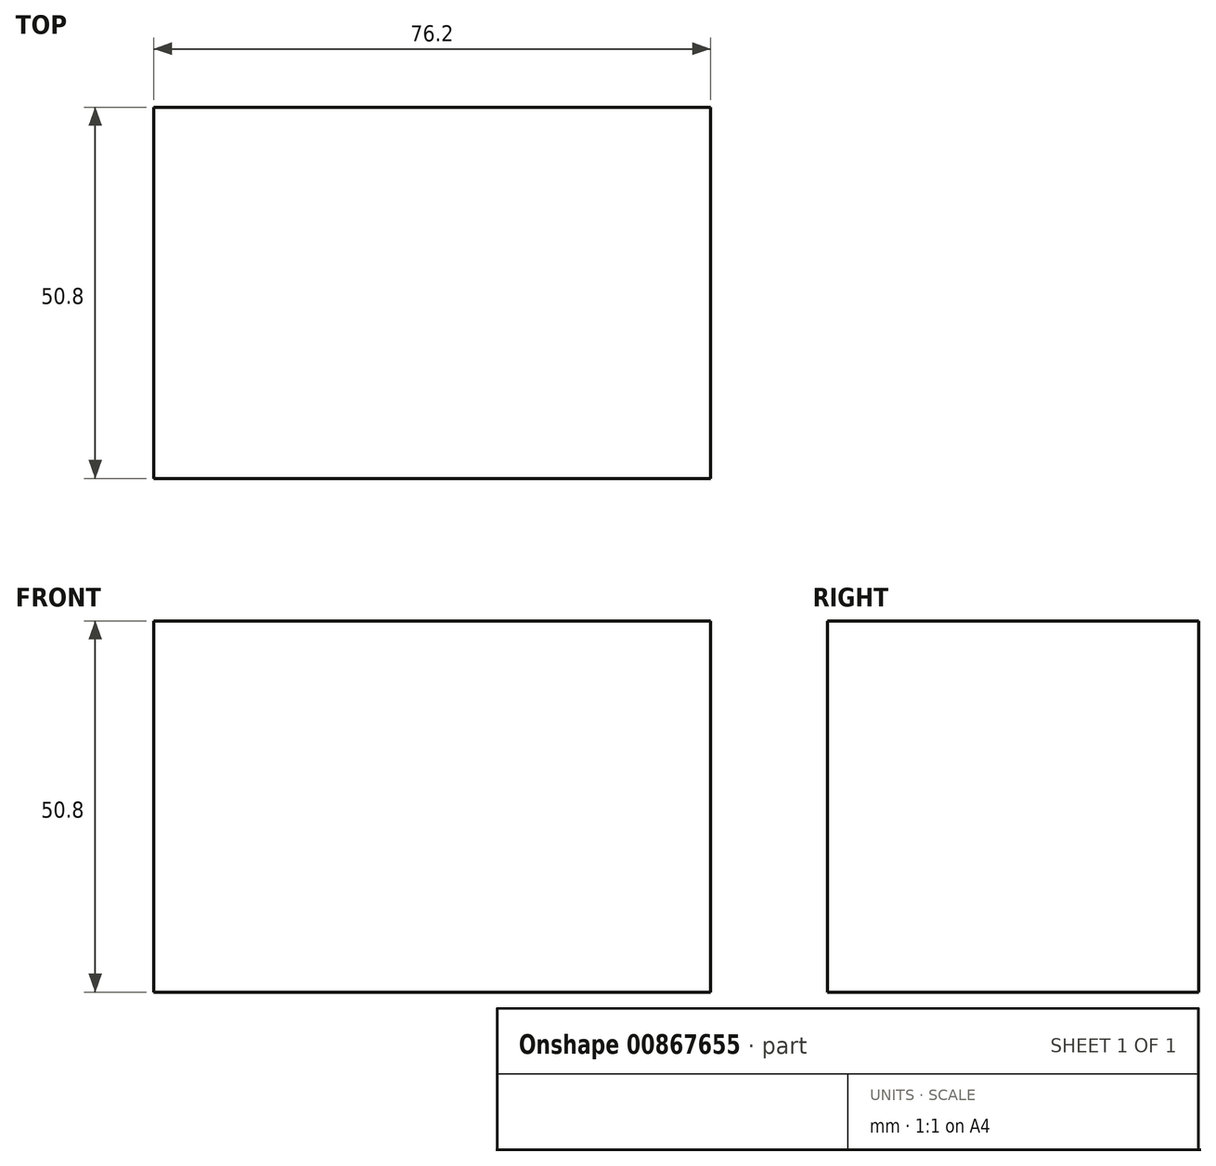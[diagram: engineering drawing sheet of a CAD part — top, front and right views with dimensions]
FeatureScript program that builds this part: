
annotation { "Feature Type Name" : "Feature", "Feature Type Description" : "" }
export const myFeature = defineFeature(function(context is Context, id is Id, definition is map)
    precondition{}
    {
        {
            var Q0;
            Q0=qCreatedBy(makeId("Front.planeOp"),FACE);
            var sketch = newSketch(context, id + "F0", { "sketchPlane" : qUnion([Q0])});
            skLineSegment(sketch, "E0.bottom", {"start": v(0, 0) * mm, "end": v(76.2, 0) * mm});
            skLineSegment(sketch, "E0.top", {"start": v(0, 50.8) * mm, "end": v(76.2, 50.8) * mm});
            skLineSegment(sketch, "E0.left", {"start": v(0, 0) * mm, "end": v(0, 50.8) * mm});
            skLineSegment(sketch, "E0.right", {"start": v(76.2, 0) * mm, "end": v(76.2, 50.8) * mm});
            skSolve(sketch);
        }
        {
            var Q0;
            Q0=makeQuery(id+"F0.imprint","IMPRINT",FACE,{"disambiguationData":[TD([[makeQuery(id+"F0.imprint","IMPRINT",EDGE,{"derivedFrom":sQuery(id+"F0.wireOp",EDGE,"E0.bottom")}),1.0]])]});
            extrude(context, id + "F1", {"entities" : qUnion([Q0]), "depth" : 50.8 * mm, "offsetDistance" : 25.4 * mm});
        }
    });
